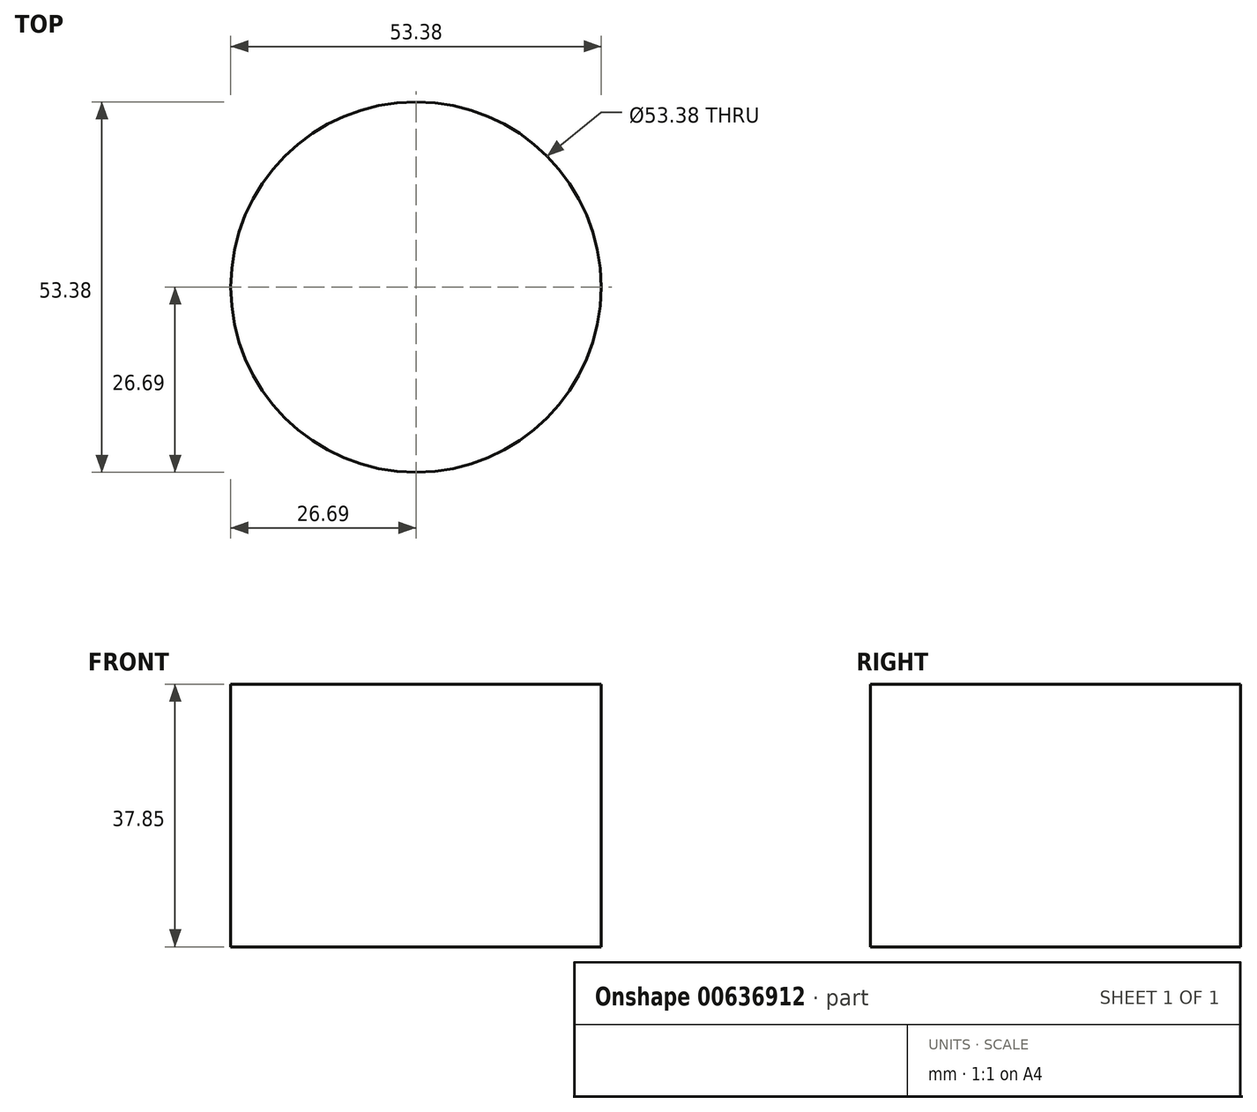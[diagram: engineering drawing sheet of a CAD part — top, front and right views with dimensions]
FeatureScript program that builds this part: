
annotation { "Feature Type Name" : "Feature", "Feature Type Description" : "" }
export const myFeature = defineFeature(function(context is Context, id is Id, definition is map)
    precondition{}
    {
        {
            var Q0;
            Q0=qCreatedBy(makeId("Top.planeOp"),FACE);
            var sketch = newSketch(context, id + "F0", { "sketchPlane" : qUnion([Q0])});
            skCircle(sketch, "E0", {"center": v(0, 0) * mm, "radius": 26.69 * mm});
            skSolve(sketch);
        }
        {
            var Q0;
            Q0=sQuery(id+"F0.wireOp",EDGE,"E0");
            extrude(context, id + "F1", {"bodyType" : ToolBodyType.SURFACE, "surfaceEntities" : qUnion([Q0]), "oppositeDirection" : true, "depth" : 37.85 * mm, "offsetDistance" : 25.4 * mm});
        }
    });
